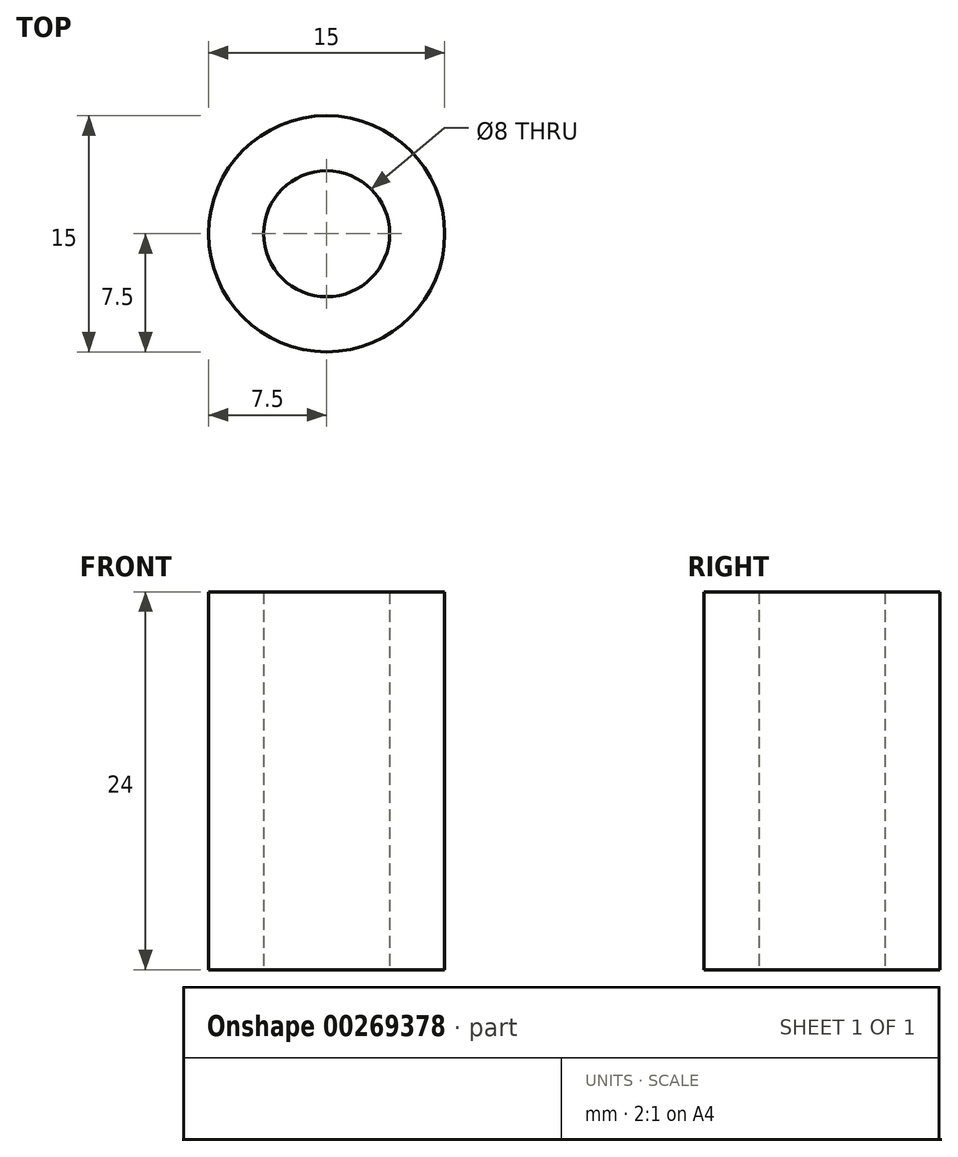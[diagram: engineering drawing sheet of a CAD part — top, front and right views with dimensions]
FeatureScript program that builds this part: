
annotation { "Feature Type Name" : "Feature", "Feature Type Description" : "" }
export const myFeature = defineFeature(function(context is Context, id is Id, definition is map)
    precondition{}
    {
        {
            var Q0;
            Q0=qCreatedBy(makeId("Top.planeOp"),FACE);
            var sketch = newSketch(context, id + "F0", { "sketchPlane" : qUnion([Q0])});
            skCircle(sketch, "E0", {"center": v(0, 0) * mm, "radius": 7.5 * mm});
            skCircle(sketch, "E1", {"center": v(0, 0) * mm, "radius": 4 * mm});
            skSolve(sketch);
        }
        {
            var Q0;
            Q0=makeQuery(id+"F0.imprint","IMPRINT",FACE,{"disambiguationData":[TD([[makeQuery(id+"F0.imprint","IMPRINT",EDGE,{"derivedFrom":sQuery(id+"F0.wireOp",EDGE,"E0")}),1.0]])]});
            extrude(context, id + "F1", {"entities" : qUnion([Q0]), "endBound" : BoundingType.SYMMETRIC, "depth" : 24 * mm});
        }
    });
